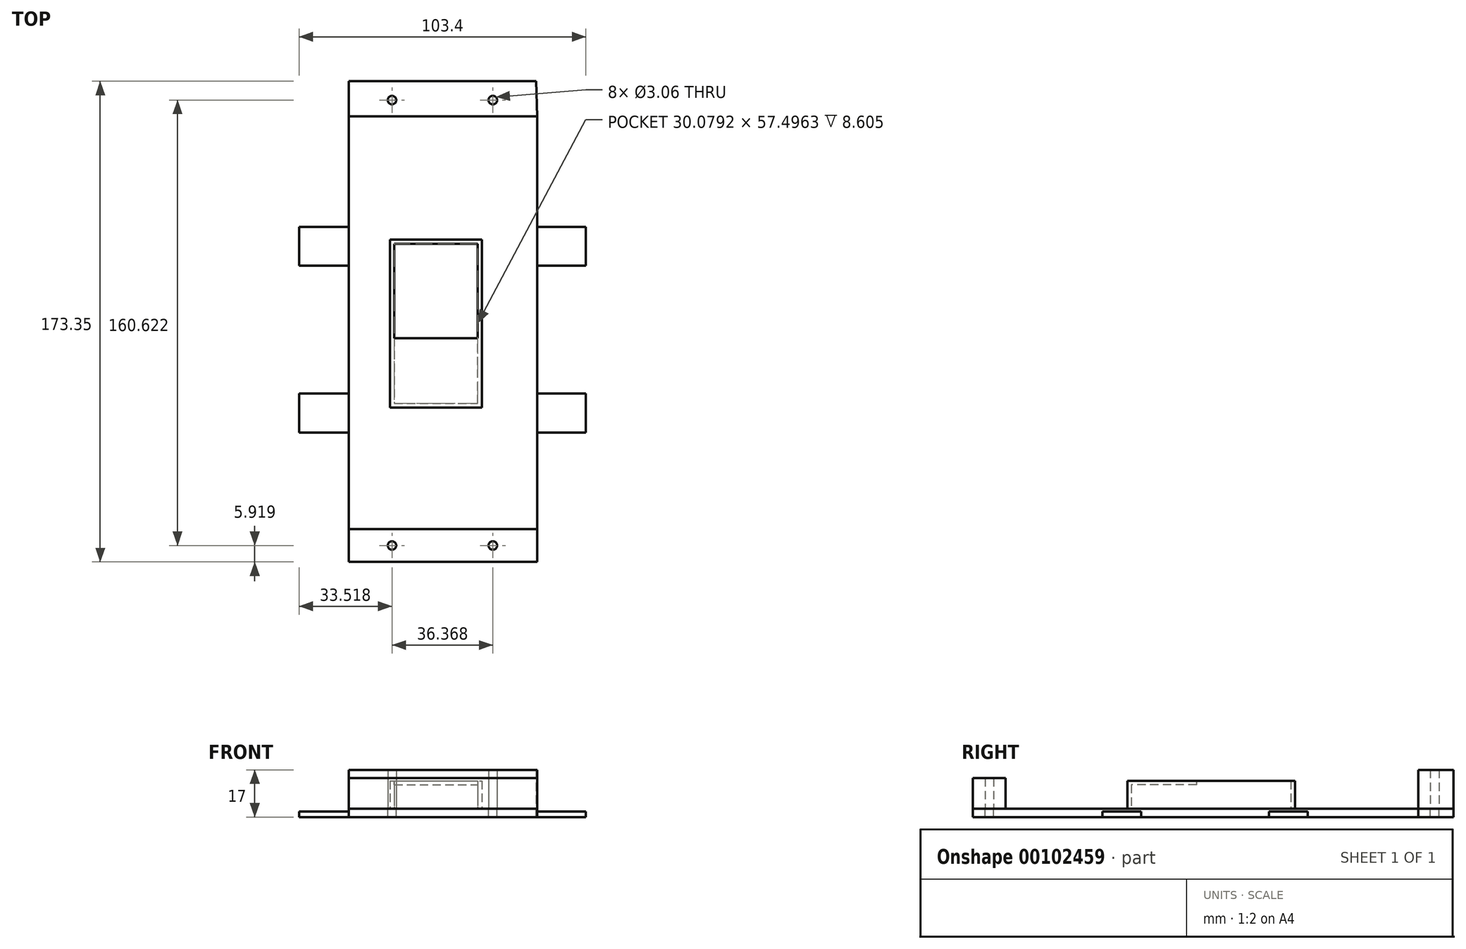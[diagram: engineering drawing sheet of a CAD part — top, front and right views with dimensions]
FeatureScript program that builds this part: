
annotation { "Feature Type Name" : "Feature", "Feature Type Description" : "" }
export const myFeature = defineFeature(function(context is Context, id is Id, definition is map)
    precondition{}
    {
        {
            var Q0;
            Q0=qCreatedBy(makeId("Top.planeOp"),FACE);
            var sketch = newSketch(context, id + "F0", { "sketchPlane" : qUnion([Q0])});
            skLineSegment(sketch, "E0.bottom", {"start": v(-91.77, 24.88) * mm, "end": v(-33.78, 24.88) * mm});
            skLineSegment(sketch, "E0.top", {"start": v(-91.77, -113.92) * mm, "end": v(-33.78, -113.92) * mm});
            skLineSegment(sketch, "E0.left", {"start": v(-91.77, 24.88) * mm, "end": v(-91.77, -113.92) * mm});
            skLineSegment(sketch, "E0.right", {"start": v(-33.78, 24.88) * mm, "end": v(-33.78, -113.92) * mm});
            skLineSegment(sketch, "E1.0", {"start": v(-28.78, 29.88) * mm, "end": v(-28.78, -118.92) * mm});
            skLineSegment(sketch, "E1.1", {"start": v(-96.77, 29.88) * mm, "end": v(-28.78, 29.88) * mm});
            skLineSegment(sketch, "E1.2", {"start": v(-96.77, 29.88) * mm, "end": v(-96.77, -118.92) * mm});
            skLineSegment(sketch, "E1.3", {"start": v(-96.77, -118.92) * mm, "end": v(-28.78, -118.92) * mm});
            skPoint(sketch, "E2.middle", {"position": v(-62.77, -44.52) * mm});
            skPoint(sketch, "E2.middle.positionSnap0", {"position": v(-62.77, 24.88) * mm});
            skPoint(sketch, "E2.centerSnap0", {"position": v(-62.77, 24.88) * mm});
            skLineSegment(sketch, "E3", {"start": v(-91.77, -113.92) * mm, "end": v(-91.77, -118.92) * mm});
            skLineSegment(sketch, "E4", {"start": v(-33.78, -113.92) * mm, "end": v(-33.78, -118.92) * mm});
            skLineSegment(sketch, "E5", {"start": v(-96.77, 29.88) * mm, "end": v(-96.77, 42.6) * mm});
            skLineSegment(sketch, "E6", {"start": v(-96.77, 42.6) * mm, "end": v(-29.25, 42.6) * mm});
            skLineSegment(sketch, "E7", {"start": v(-29.25, 42.6) * mm, "end": v(-28.78, 29.88) * mm});
            skLineSegment(sketch, "E8", {"start": v(-96.77, -118.92) * mm, "end": v(-96.77, -130.75) * mm});
            skLineSegment(sketch, "E9", {"start": v(-96.77, -130.75) * mm, "end": v(-28.78, -130.75) * mm});
            skLineSegment(sketch, "E10", {"start": v(-28.78, -130.75) * mm, "end": v(-28.78, -118.92) * mm});
            skLineSegment(sketch, "E11", {"start": v(-63, 42.6) * mm, "end": v(-63, -175.82) * mm, "construction": true});
            skCircle(sketch, "E12", {"center": v(-81.2, -124.83) * mm, "radius": 1.53 * mm});
            skPoint(sketch, "E12.centerSnap0", {"position": v(-96.77, -124.83) * mm});
            skCircle(sketch, "E13.MirrorC", {"center": v(-44.82, -124.83) * mm, "radius": 1.53 * mm});
            skCircle(sketch, "E14.MirrorC", {"center": v(-44.82, 35.8) * mm, "radius": 1.53 * mm});
            skCircle(sketch, "E15.MirrorC", {"center": v(-81.2, 35.8) * mm, "radius": 1.53 * mm});
            skLineSegment(sketch, "E16.bottom", {"start": v(-28.78, -67.58) * mm, "end": v(-18.32, -67.58) * mm});
            skLineSegment(sketch, "E16.top", {"start": v(-28.78, -21.46) * mm, "end": v(-18.32, -21.46) * mm});
            skLineSegment(sketch, "E16.left", {"start": v(-28.78, -67.58) * mm, "end": v(-28.78, -21.46) * mm});
            skLineSegment(sketch, "E16.right", {"start": v(-18.32, -67.58) * mm, "end": v(-18.32, -21.46) * mm});
            skPoint(sketch, "E16.middle", {"position": v(-23.55, -44.52) * mm});
            skLineSegment(sketch, "E17.MirrorCS", {"start": v(-97.24, -67.58) * mm, "end": v(-107.7, -67.58) * mm});
            skLineSegment(sketch, "E18.MirrorCS", {"start": v(-107.7, -67.58) * mm, "end": v(-107.7, -21.46) * mm});
            skLineSegment(sketch, "E19.MirrorCS", {"start": v(-97.24, -21.46) * mm, "end": v(-107.7, -21.46) * mm});
            skLineSegment(sketch, "E20.bottom", {"start": v(-28.78, -67.58) * mm, "end": v(-11.3, -67.58) * mm});
            skLineSegment(sketch, "E20.top", {"start": v(-28.78, -81.58) * mm, "end": v(-11.3, -81.58) * mm});
            skLineSegment(sketch, "E20.left", {"start": v(-28.78, -67.58) * mm, "end": v(-28.78, -81.58) * mm});
            skLineSegment(sketch, "E20.right", {"start": v(-11.3, -67.58) * mm, "end": v(-11.3, -81.58) * mm});
            skLineSegment(sketch, "E21.MirrorCS", {"start": v(-28.78, -21.46) * mm, "end": v(-11.3, -21.46) * mm});
            skLineSegment(sketch, "E22.MirrorCS", {"start": v(-28.78, -7.46) * mm, "end": v(-11.3, -7.46) * mm});
            skLineSegment(sketch, "E23.MirrorCS", {"start": v(-11.3, -21.46) * mm, "end": v(-11.3, -7.46) * mm});
            skLineSegment(sketch, "E24.MirrorCS", {"start": v(-97.24, -67.58) * mm, "end": v(-114.7, -67.58) * mm});
            skLineSegment(sketch, "E25.MirrorCS", {"start": v(-97.24, -81.58) * mm, "end": v(-114.7, -81.58) * mm});
            skLineSegment(sketch, "E26.MirrorCS", {"start": v(-114.7, -67.58) * mm, "end": v(-114.7, -81.58) * mm});
            skLineSegment(sketch, "E27.MirrorCS", {"start": v(-97.24, -21.46) * mm, "end": v(-114.7, -21.46) * mm});
            skLineSegment(sketch, "E28.MirrorCS", {"start": v(-114.7, -21.46) * mm, "end": v(-114.7, -7.46) * mm});
            skLineSegment(sketch, "E29.MirrorCS", {"start": v(-97.24, -7.46) * mm, "end": v(-114.7, -7.46) * mm});
            skLineSegment(sketch, "E30", {"start": v(-97.24, -21.46) * mm, "end": v(-96.77, -21.46) * mm});
            skLineSegment(sketch, "E31", {"start": v(-97.24, -7.46) * mm, "end": v(-96.77, -7.46) * mm});
            skLineSegment(sketch, "E32", {"start": v(-97.24, -67.58) * mm, "end": v(-96.77, -67.58) * mm});
            skLineSegment(sketch, "E33", {"start": v(-97.24, -81.58) * mm, "end": v(-96.77, -81.58) * mm});
            skSolve(sketch);
        }
        {
            var Q0;
            Q0=makeQuery(id+"F0.imprint","IMPRINT",FACE,{"disambiguationData":[TD([[makeQuery(id+"F0.imprint","IMPRINT",EDGE,{"derivedFrom":sQuery(id+"F0.wireOp",EDGE,"E1.1")}),1.0]])]});
            extrude(context, id + "F1", {"entities" : qUnion([Q0]), "depth" : 14 * mm});
        }
        {
            var Q0;
            {var subQ0=sQuery(id+"F0.wireOp",EDGE,"E8");Q0=makeQuery(id+"F0.imprint","IMPRINT",FACE,{"disambiguationData":[TD([[makeQuery(id+"F0.imprint","IMPRINT",EDGE,{"derivedFrom":subQ0}),1.0]])]});}
            extrude(context, id + "F2", {"entities" : qUnion([Q0]), "depth" : 11 * mm});
        }
        {
            var Q0;
            {var subQ0=sQuery(id+"F0.wireOp",EDGE,"E8");Q0=makeQuery(id+"F0.imprint","IMPRINT",FACE,{"disambiguationData":[TD([[makeQuery(id+"F0.imprint","IMPRINT",EDGE,{"derivedFrom":subQ0}),1.0]])]});}
            var sketch = newSketch(context, id + "F3", { "sketchPlane" : qUnion([Q0])});
            skLineSegment(sketch, "E34.0", {"start": v(-28.78, 29.88) * mm, "end": v(-28.78, -118.92) * mm});
            skLineSegment(sketch, "E34.1", {"start": v(-28.78, -130.75) * mm, "end": v(-28.78, -118.92) * mm});
            skLineSegment(sketch, "E34.2", {"start": v(-96.77, -130.75) * mm, "end": v(-28.78, -130.75) * mm});
            skLineSegment(sketch, "E34.3", {"start": v(-96.77, -118.92) * mm, "end": v(-96.77, -130.75) * mm});
            skLineSegment(sketch, "E34.4", {"start": v(-96.77, 29.88) * mm, "end": v(-96.77, -118.92) * mm});
            skLineSegment(sketch, "E34.5", {"start": v(-96.77, 42.6) * mm, "end": v(-29.25, 42.6) * mm});
            skLineSegment(sketch, "E34.6", {"start": v(-29.25, 42.6) * mm, "end": v(-28.78, 29.88) * mm});
            skLineSegment(sketch, "E34.7", {"start": v(-96.77, 29.88) * mm, "end": v(-96.77, 42.6) * mm});
            skCircle(sketch, "E34.8", {"center": v(-44.82, 35.8) * mm, "radius": 1.53 * mm});
            skCircle(sketch, "E34.9", {"center": v(-81.2, 35.8) * mm, "radius": 1.53 * mm});
            skCircle(sketch, "E34.10", {"center": v(-81.2, -124.83) * mm, "radius": 1.53 * mm});
            skCircle(sketch, "E34.11", {"center": v(-44.82, -124.83) * mm, "radius": 1.53 * mm});
            skSolve(sketch);
        }
        {
            var Q0;
            Q0 = qSketchRegion(id + "F3", true);
            extrude(context, id + "F4", {"entities" : qUnion([Q0]), "oppositeDirection" : true, "depth" : 3 * mm});
        }
        {
            var Q0;
            Q0=makeQuery(id+"F4.opExtrude","CAP_FACE",FACE,{"disambiguationData":[OSD([sQuery(id+"F3.wireOp",EDGE,"E34.0"),sQuery(id+"F3.wireOp",EDGE,"E34.1"),sQuery(id+"F3.wireOp",EDGE,"E34.2"),sQuery(id+"F3.wireOp",EDGE,"E34.3"),sQuery(id+"F3.wireOp",EDGE,"E34.4"),sQuery(id+"F3.wireOp",EDGE,"E34.5"),sQuery(id+"F3.wireOp",EDGE,"E34.6"),sQuery(id+"F3.wireOp",EDGE,"E34.7"),sQuery(id+"F3.wireOp",EDGE,"E34.8"),sQuery(id+"F3.wireOp",EDGE,"E34.9"),sQuery(id+"F3.wireOp",EDGE,"E34.10"),sQuery(id+"F3.wireOp",EDGE,"E34.11")])],"isStart":false});
            var sketch = newSketch(context, id + "F5", { "sketchPlane" : qUnion([Q0])});
            skPoint(sketch, "E35.0", {"position": v(-97.24, 7.46) * mm});
            skPoint(sketch, "E35.1", {"position": v(-28.78, 7.46) * mm});
            skLineSegment(sketch, "E36.0", {"start": v(-97.24, 7.46) * mm, "end": v(-114.7, 7.46) * mm});
            skLineSegment(sketch, "E37", {"start": v(-96.77, 9.96) * mm, "end": v(-114.7, 9.96) * mm});
            skLineSegment(sketch, "E38", {"start": v(-114.7, 9.96) * mm, "end": v(-114.7, 23.96) * mm});
            skLineSegment(sketch, "E39", {"start": v(-114.7, 23.96) * mm, "end": v(-96.77, 23.96) * mm});
            skPoint(sketch, "E40.0", {"position": v(-81.2, -35.8) * mm});
            skPoint(sketch, "E41.0", {"position": v(-44.82, -35.8) * mm});
            skLineSegment(sketch, "E42", {"start": v(-81.2, -35.8) * mm, "end": v(-44.82, -35.8) * mm, "construction": true});
            skLineSegment(sketch, "E43", {"start": v(-63, -35.8) * mm, "end": v(-63, 102.53) * mm, "construction": true});
            skPoint(sketch, "E44.0", {"position": v(-81.2, 124.83) * mm});
            skLineSegment(sketch, "E45.MirrorCS", {"start": v(-11.3, 23.96) * mm, "end": v(-29.25, 23.96) * mm});
            skLineSegment(sketch, "E46.MirrorCS", {"start": v(-11.3, 9.96) * mm, "end": v(-11.3, 23.96) * mm});
            skLineSegment(sketch, "E47.MirrorCS", {"start": v(-29.25, 9.96) * mm, "end": v(-11.3, 9.96) * mm});
            skLineSegment(sketch, "E48.0", {"start": v(-97.24, 67.58) * mm, "end": v(-114.7, 67.58) * mm});
            skLineSegment(sketch, "E49", {"start": v(-114.7, 70.08) * mm, "end": v(-96.77, 70.08) * mm});
            skLineSegment(sketch, "E50", {"start": v(-114.7, 70.08) * mm, "end": v(-114.7, 84.08) * mm});
            skLineSegment(sketch, "E51", {"start": v(-114.7, 84.08) * mm, "end": v(-96.77, 84.08) * mm});
            skLineSegment(sketch, "E52.MirrorCS", {"start": v(-11.3, 84.08) * mm, "end": v(-29.25, 84.08) * mm});
            skLineSegment(sketch, "E53.MirrorCS", {"start": v(-11.3, 70.08) * mm, "end": v(-11.3, 84.08) * mm});
            skLineSegment(sketch, "E54.MirrorCS", {"start": v(-11.3, 70.08) * mm, "end": v(-29.25, 70.08) * mm});
            skLineSegment(sketch, "E55", {"start": v(-96.77, 84.08) * mm, "end": v(-96.77, 9.96) * mm});
            skLineSegment(sketch, "E56", {"start": v(-29.25, 84.08) * mm, "end": v(-29.25, 9.96) * mm});
            skSolve(sketch);
        }
        {
            var Q0;
            Q0 = qSketchRegion(id + "F5", true);
            extrude(context, id + "F6", {"entities" : qUnion([Q0]), "operationType" : NewBodyOperationType.ADD, "oppositeDirection" : true, "depth" : 2 * mm});
        }
        {
            var Q0;
            Q0=makeQuery(id+"F0.imprint","IMPRINT",FACE,{"disambiguationData":[TD([[makeQuery(id+"F0.imprint","IMPRINT",EDGE,{"derivedFrom":sQuery(id+"F0.wireOp",EDGE,"E0.bottom")}),-1.0]])]});
            var sketch = newSketch(context, id + "F7", { "sketchPlane" : qUnion([Q0])});
            skLineSegment(sketch, "E57", {"start": v(-81.88, -14.56) * mm, "end": v(-48.8, -14.56) * mm});
            skLineSegment(sketch, "E58", {"start": v(-48.8, -14.56) * mm, "end": v(-48.8, -75.05) * mm});
            skLineSegment(sketch, "E59", {"start": v(-48.8, -75.05) * mm, "end": v(-81.88, -75.05) * mm});
            skLineSegment(sketch, "E60", {"start": v(-81.88, -75.05) * mm, "end": v(-81.88, -14.56) * mm});
            skLineSegment(sketch, "E61.0", {"start": v(-80.38, -16.06) * mm, "end": v(-50.3, -16.06) * mm});
            skLineSegment(sketch, "E61.1", {"start": v(-80.38, -73.55) * mm, "end": v(-80.38, -16.06) * mm});
            skLineSegment(sketch, "E61.2", {"start": v(-50.3, -73.55) * mm, "end": v(-80.38, -73.55) * mm});
            skLineSegment(sketch, "E61.3", {"start": v(-50.3, -16.06) * mm, "end": v(-50.3, -73.55) * mm});
            skSolve(sketch);
        }
        {
            var Q0;
            Q0 = qSketchRegion(id + "F7", true);
            extrude(context, id + "F8", {"entities" : qUnion([Q0]), "operationType" : NewBodyOperationType.ADD, "depth" : 10 * mm});
        }
        {
            var Q0;
            Q0=makeQuery(id+"F8.opExtrude","SWEPT_FACE",FACE,{"disambiguationData":[OSD([sQuery(id+"F7.wireOp",EDGE,"E59")])]});
            var sketch = newSketch(context, id + "F9", { "sketchPlane" : qUnion([Q0])});
            skLineSegment(sketch, "E62.bottom", {"start": v(-81.88, 10) * mm, "end": v(-48.8, 10) * mm});
            skLineSegment(sketch, "E62.top", {"start": v(-81.88, 8.6) * mm, "end": v(-48.8, 8.6) * mm});
            skLineSegment(sketch, "E62.left", {"start": v(-81.88, 10) * mm, "end": v(-81.88, 8.6) * mm});
            skLineSegment(sketch, "E62.right", {"start": v(-48.8, 10) * mm, "end": v(-48.8, 8.6) * mm});
            skSolve(sketch);
        }
        {
            var Q0;
            Q0 = qSketchRegion(id + "F9", true);
            extrude(context, id + "F10", {"entities" : qUnion([Q0]), "operationType" : NewBodyOperationType.ADD, "oppositeDirection" : true, "depth" : 25 * mm});
        }
    });
